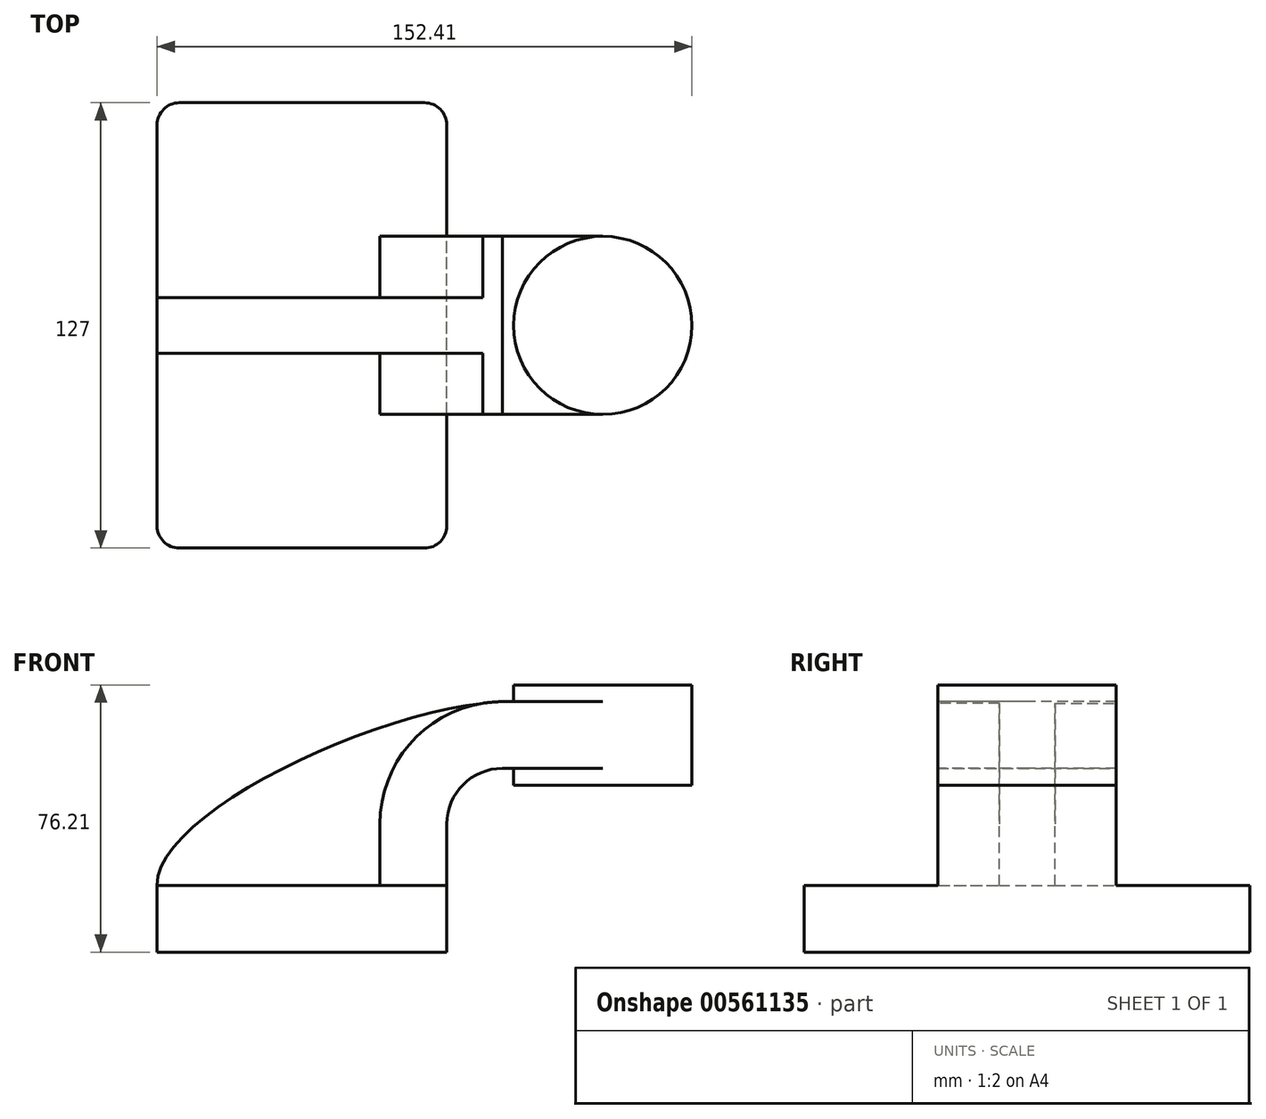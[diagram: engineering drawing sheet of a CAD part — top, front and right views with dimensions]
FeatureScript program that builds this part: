
annotation { "Feature Type Name" : "Feature", "Feature Type Description" : "" }
export const myFeature = defineFeature(function(context is Context, id is Id, definition is map)
    precondition{}
    {
        {
            var Q0;
            Q0=qCreatedBy(makeId("Front.planeOp"),FACE);
            var sketch = newSketch(context, id + "F0", { "sketchPlane" : qUnion([Q0])});
            skLineSegment(sketch, "E0.bottom", {"start": v(41.28, -9.52) * mm, "end": v(-41.28, -9.53) * mm});
            skLineSegment(sketch, "E0.top", {"start": v(41.28, 9.53) * mm, "end": v(-41.28, 9.53) * mm});
            skLineSegment(sketch, "E0.left", {"start": v(41.28, -9.52) * mm, "end": v(41.28, 9.53) * mm});
            skLineSegment(sketch, "E0.right", {"start": v(-41.28, -9.52) * mm, "end": v(-41.28, 9.53) * mm});
            skPoint(sketch, "E0.middle", {"position": v(0, 0) * mm});
            skLineSegment(sketch, "E1.bottom", {"start": v(60.32, 38.1) * mm, "end": v(111.12, 38.1) * mm});
            skLineSegment(sketch, "E1.top", {"start": v(60.32, 66.68) * mm, "end": v(111.12, 66.68) * mm});
            skLineSegment(sketch, "E1.left", {"start": v(60.32, 38.1) * mm, "end": v(60.32, 66.68) * mm});
            skLineSegment(sketch, "E1.right", {"start": v(111.12, 38.1) * mm, "end": v(111.12, 66.68) * mm});
            skPoint(sketch, "E1.middle", {"position": v(85.72, 52.39) * mm});
            skLineSegment(sketch, "E2", {"start": v(41.28, 9.53) * mm, "end": v(41.28, 27) * mm});
            skArc(sketch, "E3", {"start": v(41.27, 27) * mm, "mid": v(45.92, 38.23) * mm, "end": v(57.15, 42.88) * mm});
            skLineSegment(sketch, "E4", {"start": v(57.15, 42.88) * mm, "end": v(85.72, 42.88) * mm});
            skLineSegment(sketch, "E5.0", {"start": v(57.15, 61.93) * mm, "end": v(85.72, 61.93) * mm});
            skArc(sketch, "E5.1", {"start": v(22.23, 27) * mm, "mid": v(32.45, 51.7) * mm, "end": v(57.15, 61.93) * mm});
            skLineSegment(sketch, "E5.2", {"start": v(22.23, 9.53) * mm, "end": v(22.23, 27) * mm});
            skLineSegment(sketch, "E6", {"start": v(85.72, 38.1) * mm, "end": v(85.72, 66.68) * mm});
            skFitSpline(sketch, "E7", {"points": [v(-41.28, 9.53) * mm, v(57.15, 61.93) * mm], "startDerivative": vector(-1.2, 62.4) * mm, "endDerivative": vector(103.34, 4.3) * mm});
            skSolve(sketch);
        }
        {
            var Q0;
            Q0=makeQuery(id+"F0.imprint","IMPRINT",FACE,{"disambiguationData":[TD([[makeQuery(id+"F0.imprint","IMPRINT",EDGE,{"derivedFrom":sQuery(id+"F0.wireOp",EDGE,"E0.bottom")}),-1.0]])]});
            extrude(context, id + "F1", {"entities" : qUnion([Q0]), "endBound" : BoundingType.SYMMETRIC, "depth" : 127 * mm, "offsetDistance" : 25.4 * mm});
        }
        {
            var Q0;
            {var subQ3=sQuery(id+"F0.wireOp",EDGE,"E5.2");Q0=makeQuery(id+"F0.imprint","IMPRINT",FACE,{"disambiguationData":[TD([[makeQuery(id+"F0.imprint","IMPRINT",EDGE,{"derivedFrom":subQ3}),1.0]])]});}
            extrude(context, id + "F2", {"entities" : qUnion([Q0]), "operationType" : NewBodyOperationType.ADD, "endBound" : BoundingType.SYMMETRIC, "depth" : 15.88 * mm, "offsetDistance" : 25.4 * mm});
        }
        {
            var Q0;
            {var subQ1=sQuery(id+"F0.wireOp",EDGE,"E2");Q0=makeQuery(id+"F0.imprint","IMPRINT",FACE,{"disambiguationData":[TD([[makeQuery(id+"F0.imprint","IMPRINT",EDGE,{"derivedFrom":subQ1}),1.0]])]});}
            var Q1;
            {var subQ0=sQuery(id+"F0.wireOp",EDGE,"E4");var subQ1=sQuery(id+"F0.wireOp",EDGE,"E1.left");var subQ2=makeQuery(id+"F0.imprint","INTERSECT",VERTEX,{"derivedFrom":[subQ1,subQ0]});Q1=makeQuery(id+"F0.imprint","IMPRINT",FACE,{"disambiguationData":[TD([[makeQuery(id+"F0.imprint","IMPRINT",EDGE,{"disambiguationData":[TD([[subQ2,-1.0]])],"derivedFrom":subQ1}),-1.0]])]});}
            extrude(context, id + "F3", {"entities" : qUnion([Q0, Q1]), "operationType" : NewBodyOperationType.ADD, "endBound" : BoundingType.SYMMETRIC, "depth" : 50.8 * mm, "offsetDistance" : 25.4 * mm});
        }
        {
            var Q0;
            {var subQ4=sQuery(id+"F0.wireOp",EDGE,"E1.right");Q0=makeQuery(id+"F0.imprint","IMPRINT",FACE,{"disambiguationData":[TD([[makeQuery(id+"F0.imprint","IMPRINT",EDGE,{"derivedFrom":subQ4}),1.0]])]});}
            var Q1;
            Q1=sQuery(id+"F0.wireOp",EDGE,"E6");
            revolve(context, id + "F4", {"operationType" : NewBodyOperationType.ADD, "entities" : qUnion([Q0]), "axis" : qUnion([Q1]), "revolveType" : RevolveType.FULL});
        }
        {
            var Q0;
            Q0=makeQuery(id+"F1.opExtrude","CAP_EDGE",EDGE,{"disambiguationData":[OSD([sQuery(id+"F0.wireOp",EDGE,"E0.left")])],"isStart":false});
            var Q1;
            Q1=makeQuery(id+"F1.opExtrude","CAP_EDGE",EDGE,{"disambiguationData":[OSD([sQuery(id+"F0.wireOp",EDGE,"E0.right")])],"isStart":false});
            var Q2;
            Q2=makeQuery(id+"F1.opExtrude","CAP_EDGE",EDGE,{"disambiguationData":[OSD([sQuery(id+"F0.wireOp",EDGE,"E0.right")])],"isStart":true});
            var Q3;
            Q3=makeQuery(id+"F1.opExtrude","CAP_EDGE",EDGE,{"disambiguationData":[OSD([sQuery(id+"F0.wireOp",EDGE,"E0.left")])],"isStart":true});
            fillet(context, id + "F5", {"entities" : qUnion([Q0, Q1, Q2, Q3]), "radius" : 6.35 * mm, "tangentPropagation" : true, "allowEdgeOverflow" : false});
        }
    });
